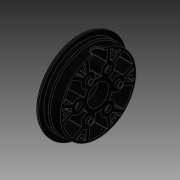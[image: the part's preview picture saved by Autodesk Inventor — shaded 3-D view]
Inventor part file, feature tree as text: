
AUTODESK INVENTOR PART (.ipt)
format: ipt  version: 2014 SP1 (Build 180222100, 222)  size: 754,176 bytes
history: native  units: in
note: dims shown in document units (in); Inventor stores cm internally (conversion verified against a paired STEP export)
features: fillet x1, other x1, imported_body x1
ambient origin geometry x8: Origin, YZ Plane, XZ Plane, XY Plane, X Axis, Y Axis, Z Axis, Center Point
bodies: Body1 (feature_tree)
feature tree (3):
  fillet  "Fillet7"  [1 undecoded]
  other  "Hub1"
  imported_body  "Base1"
note: 1 required parameter value undecoded (feature->parameter linkage not recoverable at this tier; creation-order binding heuristic only, values carry confidence <= 0.55)
